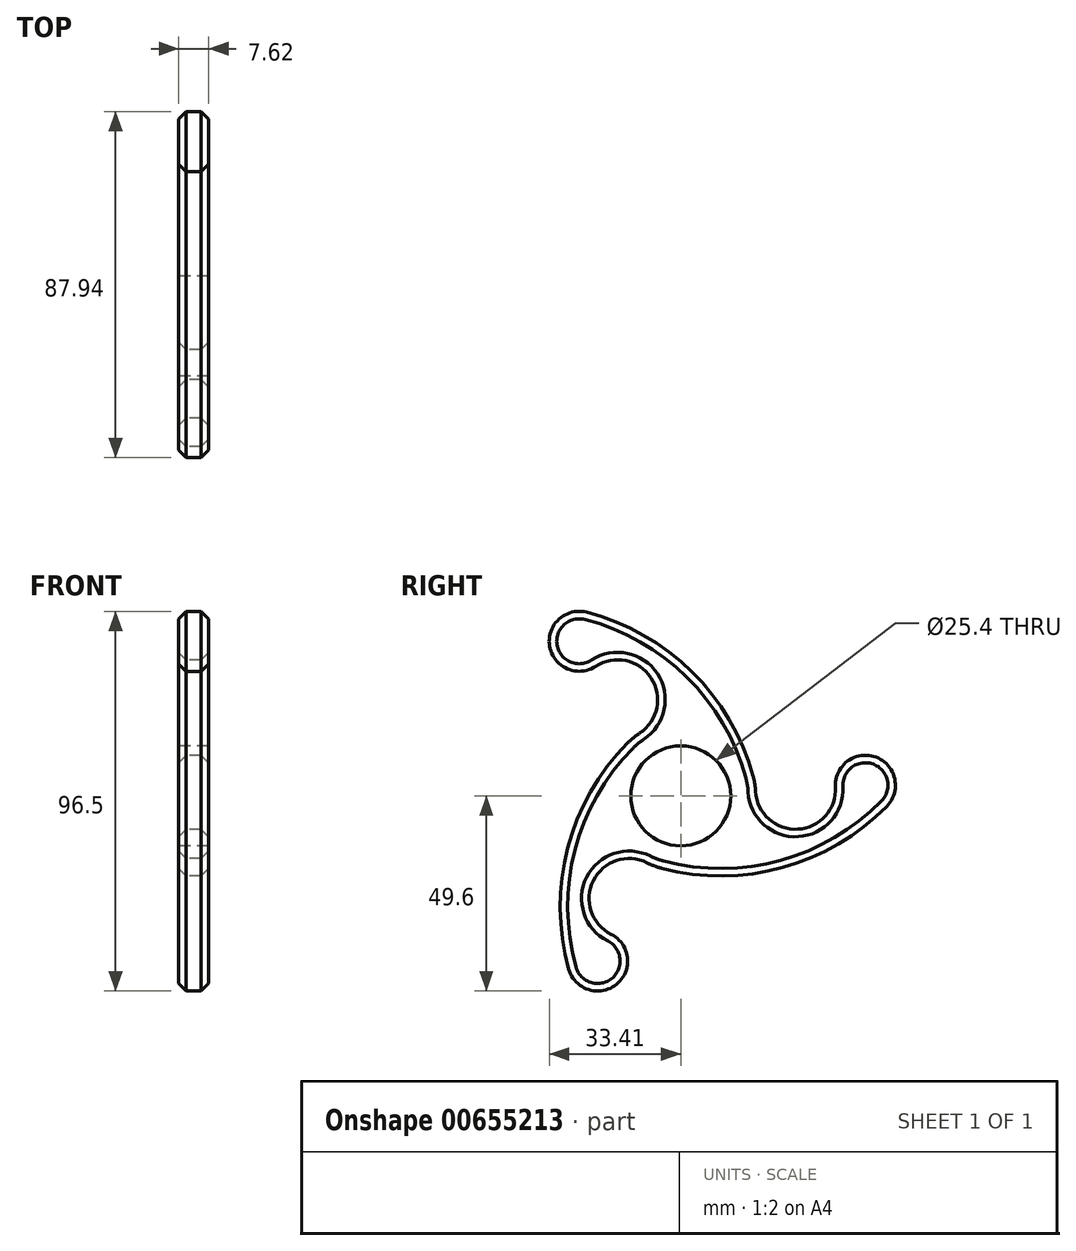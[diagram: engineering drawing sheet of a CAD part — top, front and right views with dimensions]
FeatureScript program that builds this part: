
annotation { "Feature Type Name" : "Feature", "Feature Type Description" : "" }
export const myFeature = defineFeature(function(context is Context, id is Id, definition is map)
    precondition{}
    {
        {
            var Q0;
            Q0=qCreatedBy(makeId("Right.planeOp"),FACE);
            var sketch = newSketch(context, id + "F0", { "sketchPlane" : qUnion([Q0])});
            skCircle(sketch, "E0", {"center": v(0, 0) * mm, "radius": 19.05 * mm});
            skCircle(sketch, "E1", {"center": v(0, 0) * mm, "radius": 12.7 * mm});
            skCircle(sketch, "E2", {"center": v(46.91, 2.7) * mm, "radius": 7.62 * mm});
            skArc(sketch, "E3", {"start": v(-4.82, -18.43) * mm, "mid": v(25.89, -18.22) * mm, "end": v(52.35, -2.64) * mm});
            skArc(sketch, "E4", {"start": v(19.02, 1.1) * mm, "mid": v(29.75, -8.47) * mm, "end": v(39.3, 2.26) * mm});
            skArc(sketch, "E5.1.0", {"start": v(-10.46, 15.92) * mm, "mid": v(-7.54, 30) * mm, "end": v(-21.61, 32.9) * mm});
            skArc(sketch, "E5.1.1", {"start": v(18.37, 5.04) * mm, "mid": v(2.83, 31.53) * mm, "end": v(-23.9, 46.66) * mm});
            skCircle(sketch, "E5.1.2", {"center": v(-25.8, 39.28) * mm, "radius": 7.62 * mm});
            skArc(sketch, "E5.2.0", {"start": v(-8.56, -17.02) * mm, "mid": v(-22.2, -21.53) * mm, "end": v(-17.7, -35.17) * mm});
            skArc(sketch, "E5.2.1", {"start": v(-13.55, 13.39) * mm, "mid": v(-28.72, -13.31) * mm, "end": v(-28.46, -44.02) * mm});
            skCircle(sketch, "E5.2.2", {"center": v(-21.12, -41.98) * mm, "radius": 7.62 * mm});
            skSolve(sketch);
        }
        {
            var Q0;
            Q0=qSketchRegion(id+"F0",true);
            extrude(context, id + "F1", {"entities" : qUnion([Q0]), "depth" : 7.62 * mm, "offsetDistance" : 25.4 * mm});
        }
        {
            var Q0;
            Q0=makeQuery(id+"F1.opExtrude","CAP_EDGE",EDGE,{"disambiguationData":[OSD([sQuery(id+"F0.wireOp",EDGE,"E3")])],"isStart":true});
            var Q1;
            Q1=makeQuery(id+"F1.opExtrude","CAP_EDGE",EDGE,{"disambiguationData":[OSD([sQuery(id+"F0.wireOp",EDGE,"E4")])],"isStart":true});
            var Q2;
            Q2=makeQuery(id+"F1.opExtrude","CAP_EDGE",EDGE,{"disambiguationData":[OSD([sQuery(id+"F0.wireOp",EDGE,"E3")])],"isStart":false});
            chamfer(context, id + "F2", {"entities" : qUnion([Q0, Q1, Q2]), "width" : 1.9 * mm, "tangentPropagation" : true});
        }
    });
